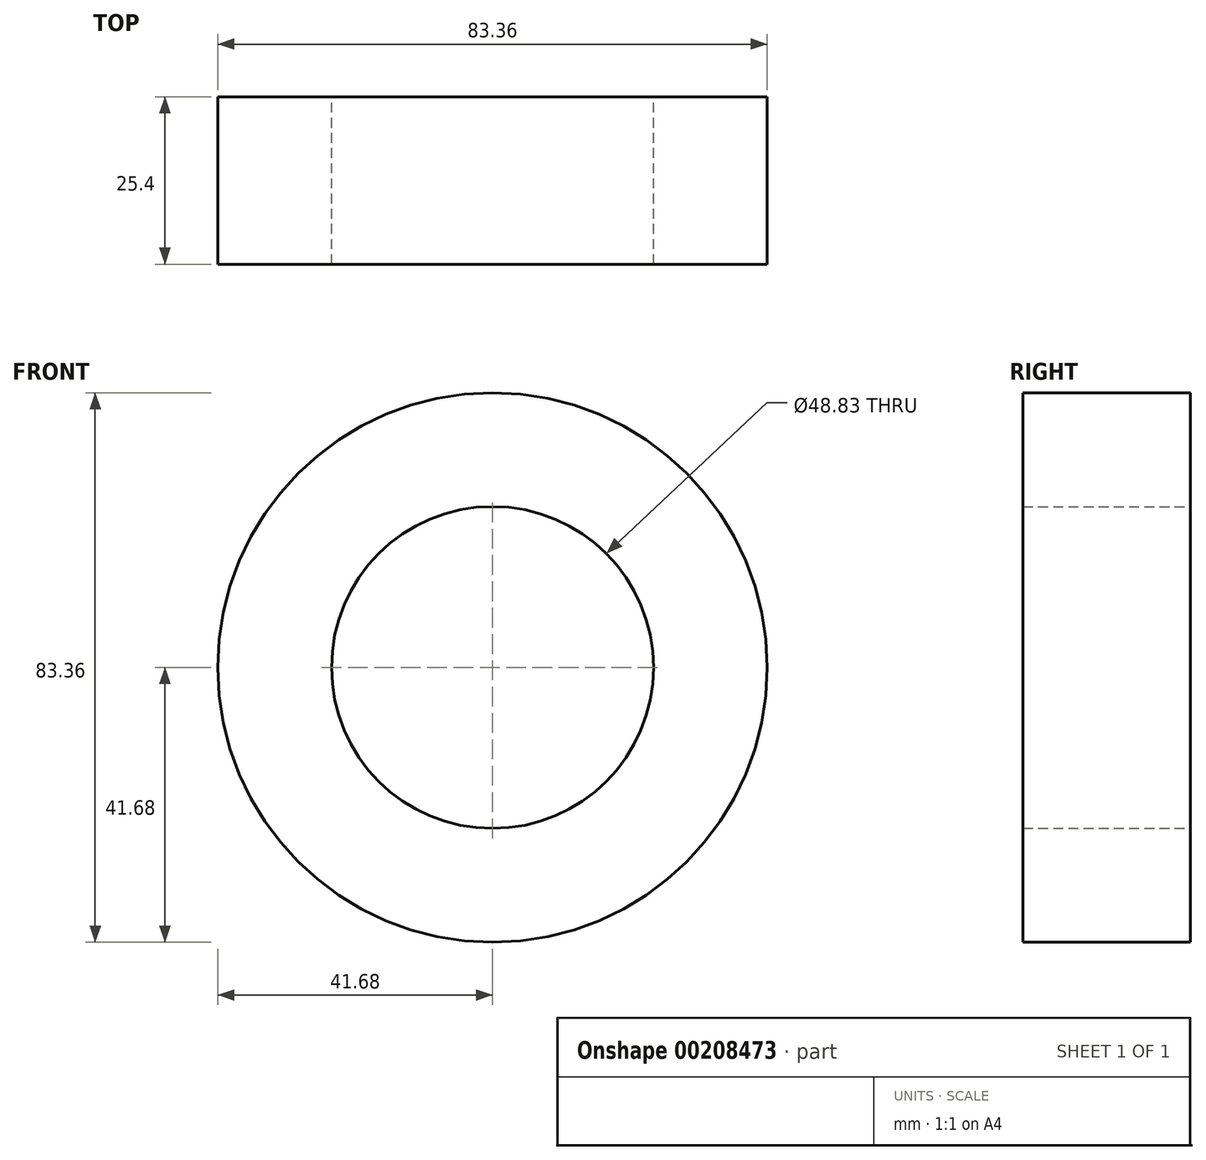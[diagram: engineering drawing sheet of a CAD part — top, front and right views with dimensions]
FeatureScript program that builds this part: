
annotation { "Feature Type Name" : "Feature", "Feature Type Description" : "" }
export const myFeature = defineFeature(function(context is Context, id is Id, definition is map)
    precondition{}
    {
        {
            var Q0;
            Q0=qCreatedBy(makeId("Front.planeOp"),FACE);
            var sketch = newSketch(context, id + "F0", { "sketchPlane" : qUnion([Q0])});
            skCircle(sketch, "E0", {"center": v(0, 0) * mm, "radius": 41.68 * mm});
            skCircle(sketch, "E1", {"center": v(0, 0) * mm, "radius": 24.41 * mm});
            skSolve(sketch);
        }
        {
            var Q0;
            Q0 = qSketchRegion(id + "F0", true);
            extrude(context, id + "F1", {"entities" : qUnion([Q0]), "depth" : 25.4 * mm});
        }
    });
